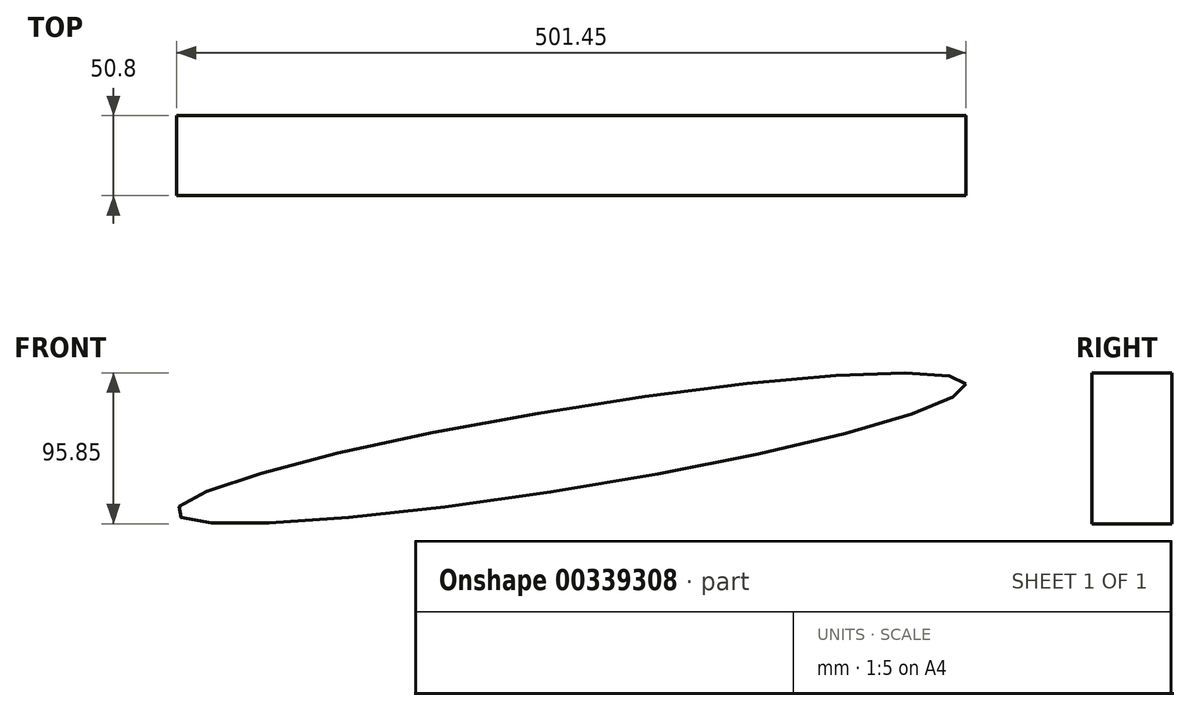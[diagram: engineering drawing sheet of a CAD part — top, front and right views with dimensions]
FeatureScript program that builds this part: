
annotation { "Feature Type Name" : "Feature", "Feature Type Description" : "" }
export const myFeature = defineFeature(function(context is Context, id is Id, definition is map)
    precondition{}
    {
        {
            var Q0;
            Q0=qCreatedBy(makeId("Front.planeOp"),FACE);
            var sketch = newSketch(context, id + "F0", { "sketchPlane" : qUnion([Q0])});
            skEllipse(sketch, "E0", {"center": v(-65.5, 24.1) * mm, "majorRadius": 254 * mm, "minorRadius": 25.4 * mm, "majorAxis": v(0.99, 0.16)});
            skSolve(sketch);
        }
        {
            var Q0;
            Q0 = qSketchRegion(id + "F0", true);
            extrude(context, id + "F1", {"entities" : qUnion([Q0]), "depth" : 50.8 * mm});
        }
    });
